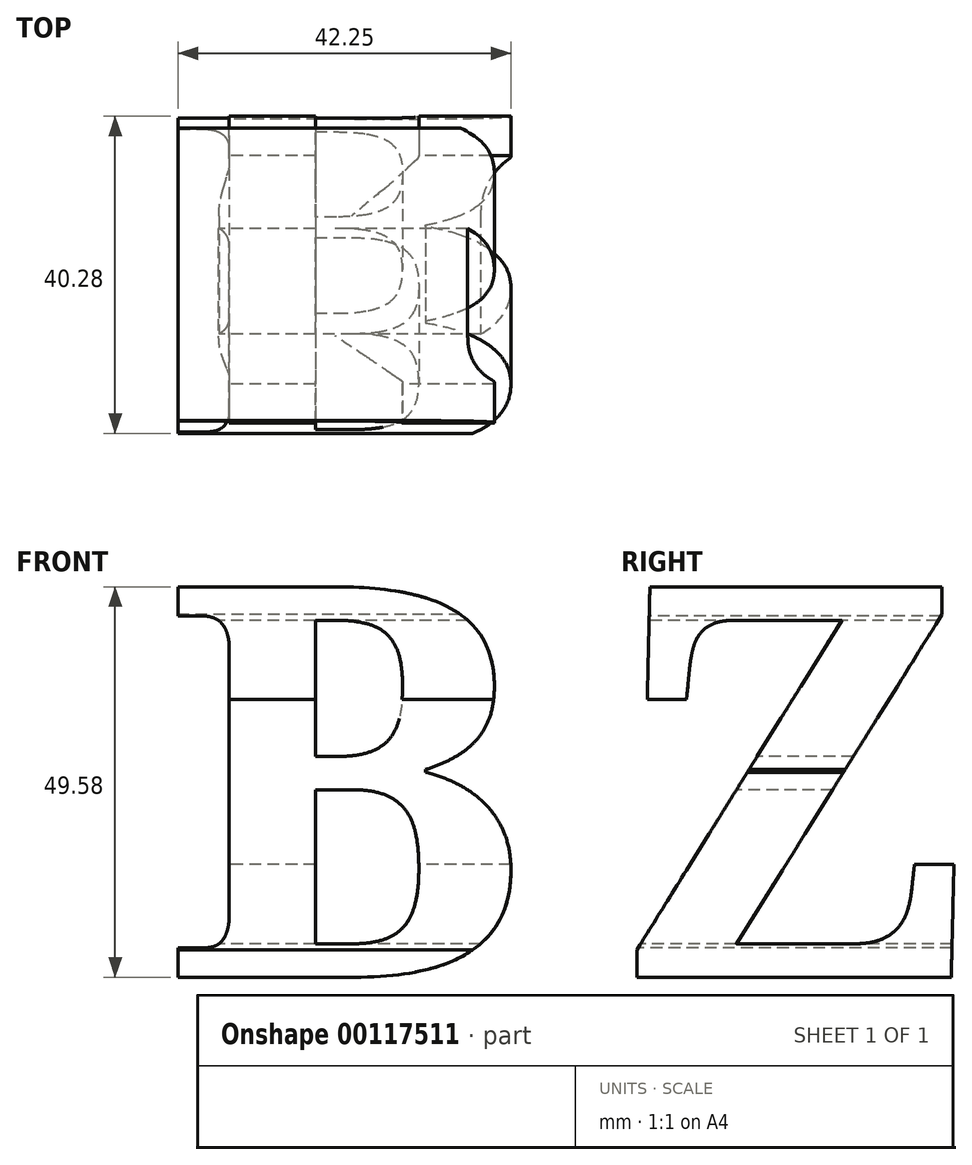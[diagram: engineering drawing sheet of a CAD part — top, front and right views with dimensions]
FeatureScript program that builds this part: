
annotation { "Feature Type Name" : "Feature", "Feature Type Description" : "" }
export const myFeature = defineFeature(function(context is Context, id is Id, definition is map)
    precondition{}
    {
        {
            var Q0;
            Q0=qCreatedBy(makeId("Front.planeOp"),FACE);
            var sketch = newSketch(context, id + "F0", { "sketchPlane" : qUnion([Q0])});
            skText(sketch, "E0", { "text": "B", "fontName": "NotoSerif-Bold.ttf"});
            const initialGuessF0  = {"E0": [0, 0, 1, 0, 0.05]};
            skSetInitialGuess(sketch, initialGuessF0);
            skSolve(sketch);
        }
        {
            var Q0;
            Q0=qCreatedBy(makeId("Right.planeOp"),FACE);
            var sketch = newSketch(context, id + "F1", { "sketchPlane" : qUnion([Q0])});
            skText(sketch, "E1", { "text": "Z", "fontName": "NotoSerif-Bold.ttf"});
            const initialGuessF1  = {"E1": [0, 0, 1, 0, 0.05]};
            skSetInitialGuess(sketch, initialGuessF1);
            skSolve(sketch);
        }
        {
            var Q0;
            Q0=makeQuery(id+"F1.imprint","IMPRINT",FACE,{"disambiguationData":[TD([[makeQuery(id+"F1.imprint","IMPRINT",EDGE,{"derivedFrom":sQuery(id+"F1.wireOp",EDGE,"E1.sketch_text.stroke-0")}),-1.0]])]});
            extrude(context, id + "F2", {"entities" : qUnion([Q0]), "depth" : 50 * mm});
        }
        {
            var Q0;
            Q0=makeQuery(id+"F0.imprint","IMPRINT",FACE,{"disambiguationData":[TD([[makeQuery(id+"F0.imprint","IMPRINT",EDGE,{"derivedFrom":sQuery(id+"F0.wireOp",EDGE,"E0.sketch_text.stroke-0")}),-1.0]])]});
            extrude(context, id + "F3", {"entities" : qUnion([Q0]), "oppositeDirection" : true, "depth" : 50 * mm});
        }
        {
            var Q0;
            Q0=makeQuery(id+"F2.opExtrude","SWEPT_BODY",BODY,{"disambiguationData":[OSD([sQuery(id+"F1.wireOp",EDGE,"E1.sketch_text.stroke-0"),sQuery(id+"F1.wireOp",EDGE,"E1.sketch_text.stroke-1"),sQuery(id+"F1.wireOp",EDGE,"E1.sketch_text.stroke-2"),sQuery(id+"F1.wireOp",EDGE,"E1.sketch_text.stroke-3"),sQuery(id+"F1.wireOp",EDGE,"E1.sketch_text.stroke-4"),sQuery(id+"F1.wireOp",EDGE,"E1.sketch_text.stroke-5"),sQuery(id+"F1.wireOp",EDGE,"E1.sketch_text.stroke-6"),sQuery(id+"F1.wireOp",EDGE,"E1.sketch_text.stroke-7"),sQuery(id+"F1.wireOp",EDGE,"E1.sketch_text.stroke-8"),sQuery(id+"F1.wireOp",EDGE,"E1.sketch_text.stroke-9")])]});
            var Q1;
            Q1=makeQuery(id+"F3.opExtrude","SWEPT_BODY",BODY,{"disambiguationData":[OSD([sQuery(id+"F0.wireOp",EDGE,"E0.sketch_text.stroke-0"),sQuery(id+"F0.wireOp",EDGE,"E0.sketch_text.stroke-1"),sQuery(id+"F0.wireOp",EDGE,"E0.sketch_text.stroke-2"),sQuery(id+"F0.wireOp",EDGE,"E0.sketch_text.stroke-3"),sQuery(id+"F0.wireOp",EDGE,"E0.sketch_text.stroke-4"),sQuery(id+"F0.wireOp",EDGE,"E0.sketch_text.stroke-5"),sQuery(id+"F0.wireOp",EDGE,"E0.sketch_text.stroke-6"),sQuery(id+"F0.wireOp",EDGE,"E0.sketch_text.stroke-7"),sQuery(id+"F0.wireOp",EDGE,"E0.sketch_text.stroke-8"),sQuery(id+"F0.wireOp",EDGE,"E0.sketch_text.stroke-9"),sQuery(id+"F0.wireOp",EDGE,"E0.sketch_text.stroke-10"),sQuery(id+"F0.wireOp",EDGE,"E0.sketch_text.stroke-11"),sQuery(id+"F0.wireOp",EDGE,"E0.sketch_text.stroke-12"),sQuery(id+"F0.wireOp",EDGE,"E0.sketch_text.stroke-13"),sQuery(id+"F0.wireOp",EDGE,"E0.sketch_text.stroke-14"),sQuery(id+"F0.wireOp",EDGE,"E0.sketch_text.stroke-15"),sQuery(id+"F0.wireOp",EDGE,"E0.sketch_text.stroke-16"),sQuery(id+"F0.wireOp",EDGE,"E0.sketch_text.stroke-17"),sQuery(id+"F0.wireOp",EDGE,"E0.sketch_text.stroke-18"),sQuery(id+"F0.wireOp",EDGE,"E0.sketch_text.stroke-19"),sQuery(id+"F0.wireOp",EDGE,"E0.sketch_text.stroke-20"),sQuery(id+"F0.wireOp",EDGE,"E0.sketch_text.stroke-21"),sQuery(id+"F0.wireOp",EDGE,"E0.sketch_text.stroke-22"),sQuery(id+"F0.wireOp",EDGE,"E0.sketch_text.stroke-23"),sQuery(id+"F0.wireOp",EDGE,"E0.sketch_text.stroke-24")])]});
            booleanBodies(context, id + "F4", {"operationType" : BooleanOperationType.INTERSECTION, "tools" : qUnion([Q0, Q1])});
        }
    });
